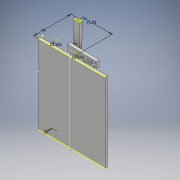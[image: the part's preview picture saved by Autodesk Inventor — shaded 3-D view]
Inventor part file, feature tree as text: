
AUTODESK INVENTOR PART (.ipt)
format: ipt  version: 2017 (Build 210142000, 142)  size: 602,112 bytes
history: native  units: mm
features: sketch x43, extrude x30, plane x9, projected_geometry x4, pattern_linear x3, other x1, sweep x1, fillet x1
ambient origin geometry x8: Origin, YZ Plane, XZ Plane, XY Plane, X Axis, Y Axis, Z Axis, Center Point
bodies: Body1 (feature_tree), Body2 (feature_tree)
feature tree (92):
  other  "實體1"
  extrude  "擠出1"  Depth=200.0mm
  sketch  "草圖2"
  sketch  "草圖4"
  plane  "工作平面2"
  sketch  "草圖5"
  extrude  "擠出2"  Depth=170.0mm
  extrude  "擠出3"  Depth=5.0mm TaperAngle=0.0deg
  extrude  "擠出4"  Depth=94.0mm
  sketch  "草圖8"
  sketch  "草圖9"
  plane  "工作平面4"
  sketch  "草圖11"
  extrude  "擠出5"  Depth=10.0mm
  extrude  "擠出6"  Depth=89.0mm
  extrude  "擠出7"  Depth=10.0mm
  sketch  "草圖13"
  sketch  "草圖14"
  plane  "工作平面5"
  sketch  "草圖15"
  extrude  "擠出8"  Depth=60.0mm
  extrude  "擠出9"  Depth=15.0mm
  extrude  "擠出10"  Depth=1.5mm
  sketch  "草圖17"
  sketch  "草圖18"
  plane  "工作平面7"
  sketch  "草圖20"
  extrude  "擠出11"  Depth=1.5mm
  extrude  "擠出12"  Depth=1.5mm
  extrude  "擠出13"  Depth=7.0mm TaperAngle=0.0deg
  sketch  "草圖22"
  sketch  "草圖23"
  plane  "工作平面8"
  sketch  "草圖24"
  extrude  "擠出14"  Depth=6.0mm TaperAngle=0.0deg
  extrude  "擠出15"  Depth=12.0mm
  sketch  "草圖29"
  sketch  "草圖30"
  plane  "工作平面10"
  extrude  "擠出17"  Depth=5.0mm TaperAngle=0.0deg
  extrude  "擠出18"  Depth=74.0mm
  extrude  "擠出26"  Depth=79.0mm
  plane  "工作平面16"
  extrude  "擠出27"  Depth=75.0mm
  extrude  "擠出28"  Depth=15.0mm
  extrude  "擠出29"  Depth=1.5mm
  extrude  "擠出19"  Depth=1.0mm
  extrude  "擠出20"  Depth=7.0mm TaperAngle=0.0deg
  pattern_linear  "矩形陣列1"  Spacing1=6.0mm  [1 undecoded]
  extrude  "擠出21"  Depth=12.0mm
  pattern_linear  "矩形陣列2"  Spacing1=7.0mm  [1 undecoded]
  extrude  "擠出22"  Depth=64.0mm
  extrude  "擠出23"  Depth=59.0mm
  extrude  "擠出24"  Depth=15.0mm
  sketch  "草圖39"
  sketch  "草圖40"
  plane  "工作平面11"
  sketch  "草圖42"
  plane  "工作平面14"
  sweep  "掃掠1"
  extrude  "擠出25"  Depth=1.5mm
  sketch  "草圖46"
  extrude  "擠出30"  Depth=70.0mm
  extrude  "擠出31"  Depth=7.0mm TaperAngle=0.0deg
  fillet  "圓角1"  Radius=6.0mm
  sketch  "草圖54"
  pattern_linear  "矩形陣列4"  Spacing1=6.0mm  [1 undecoded]
  sketch  "草圖1"
  sketch  "草圖7"
  sketch  "草圖12"
  sketch  "草圖16"
  sketch  "草圖21"
  sketch  "草圖31"
  sketch  "草圖32"
  projected_geometry  "投影迴路2"
  sketch  "草圖33"
  projected_geometry  "投影迴路3"
  sketch  "草圖34"
  sketch  "草圖35"
  sketch  "草圖36"
  sketch  "草圖37"
  sketch  "草圖38"
  projected_geometry  "投影迴路4"
  sketch  "草圖44"
  sketch  "草圖45"
  sketch  "草圖47"
  sketch  "草圖49"
  sketch  "草圖50"
  sketch  "草圖51"
  sketch  "草圖52"
  sketch  "草圖53"
  projected_geometry  "投影迴路5"
note: 3 required parameter values undecoded (feature->parameter linkage not recoverable at this tier; creation-order binding heuristic only, values carry confidence <= 0.55)
